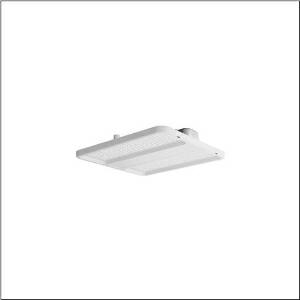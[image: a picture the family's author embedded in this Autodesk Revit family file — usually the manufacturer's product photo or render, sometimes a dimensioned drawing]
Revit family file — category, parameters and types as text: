
# Revit family: highbay_21_midi_52hn12da4hda
name_source: partatom
category: Lighting Fixtures
units: mm (PartAtom-declared; Revit-internal decimal feet)

## family parameters
Cut with Voids When Loaded = No
Host = Face
Light Source = No
Part Type = Normal
Room Calculation Point = No
Round Connector Dimension = Use Diameter
Shared = No

## types (1)
- --- (1 x LED, 2910 lm, 15.9 W, 4000K)
    Apparent Load = 16 VA
    CIE Flux Codes = 90 98 100 100 100
    Color Rendering = 80
    Color Temperature = 4000K
    Default Elevation = 1800 mm
    Description = high bay luminaire Highbay 21 midi; direct symmetric wide distribution, light control with lens of PMMA; UGR ≤ 22 (X = 4H | Y = 8H | S = 0.25H | reflection values 70/50/20); luminous flux: 19.000lm; light colour: 840, colour temperature: 4000K, MacAdam ≤ 3 SDCM (initial), colour rendering: CRI > 80; luminous efficacy: 192,1lm/W; rated service life: 75.000h (L80/B50) at AT= ta max; control: DALI 2; housing frame of high-performance plastic PA6, matt traffic white (RAL 9016); cover of PMMA; dimension (LxWxH): 474 x 442 x 72mm; luminaire connection: terminal, 5-pole, max. 2.5mm² (cable entry for one cable, Ø 8.5..16mm); mains connection: 230..240V, AC/DC 0/50..60Hz; connected load: 98,9W; protection rating (complete): IP66; insulation class (complete): insulation class I (protective earthing); protection symbol: D; impact resistance: IK08; halogen-free wiring; for central battery installations according to DIN EN 60598-2-22; LABS conformity tested according to VDMA 24364:2018-05; corresponds to IFS (International Featured Standards) requirements for safety and quality in the food industry; certification: CE, ENEC, VDE, UKCA; permissible operating ambient temperature: -40..+60°C (reducing of maximum allowable ambient temperature of 5°C with ceiling mounting); packaging unit: 1 piece; (delivery without accessories; please order mounting accessories separately)
    Height = 72 mm  [stored 0.23622 ft]
    Lamp = 1 x LED
    Lamp Light Flux = 2910 lm
    Lamp Power = 15.9 W
    Lamp count = 1
    Length = 474 mm
    Luminous efficacy = 183 lm/W
    Manufacturer = Siteco
    ModVariant = No
    Model = 52HN12DA4HDA
    Mounting Place = Ceiling
    Mounting Type = Pendant
    Number of Poles = 1
    OnlyDefault = Yes
    Power Factor = 1
    Product Name = Highbay 21 midi
    Product group = high bay luminaire
    ProductGroupID = 901
    Protection Class = Protection class I
    Protection Degree = IP 66
    RLX_Detail_Level = 1
    RLX_Emergency_Light_Flux = 0 lm
    RLX_Emergency_Type = 0
    RLX_Emergency_Type_DB = No
    RlxData = <blob elided: 17533 chars, md5=56b64b17>
    Socket = socket
    Standby Power = 0 W
    System Light Flux = 2910 lm
    System Power = 16 W
    Type Comments = : DC mode (central or group accumulator) initial emergency light level
    Type Image = l_1363240.jpg
    URL = http://relux.com
    VarID = @adj_000567
    Voltage = 0 V
    Weight = 0.00 kg
    Width = 442 mm

note: [stored X ft] marks values corroborated as IEEE doubles in the binary element streams (Revit-internal decimal feet)

## geometry (parser evidence)
native form markers: Blend x4, Sweep x10
no freeform markers — native parametric forms only
